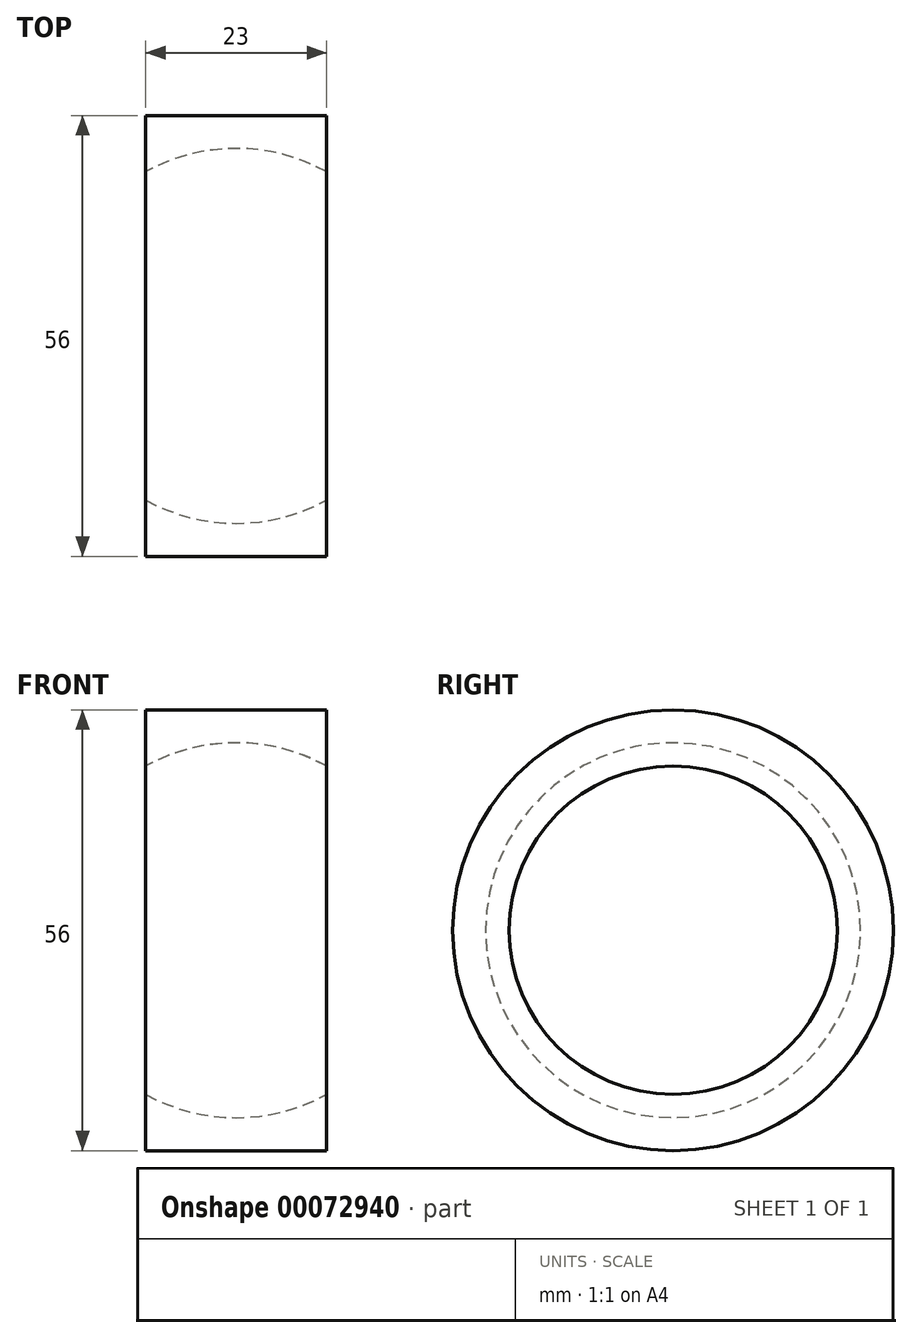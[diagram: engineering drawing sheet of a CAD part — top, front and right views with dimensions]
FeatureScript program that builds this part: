
annotation { "Feature Type Name" : "Feature", "Feature Type Description" : "" }
export const myFeature = defineFeature(function(context is Context, id is Id, definition is map)
    precondition{}
    {
        {
            var Q0;
            Q0=qCreatedBy(makeId("Top.planeOp"),FACE);
            var sketch = newSketch(context, id + "F0", { "sketchPlane" : qUnion([Q0])});
            skArc(sketch, "E0", {"start": v(11.5, 20.85) * mm, "mid": v(0, 23.81) * mm, "end": v(-11.5, 20.85) * mm});
            skLineSegment(sketch, "E1", {"start": v(-11.5, 20.85) * mm, "end": v(-11.5, 28) * mm});
            skLineSegment(sketch, "E2", {"start": v(-11.5, 28) * mm, "end": v(11.5, 28) * mm});
            skLineSegment(sketch, "E3", {"start": v(11.5, 28) * mm, "end": v(11.5, 20.85) * mm});
            skLineSegment(sketch, "E4", {"start": v(-56.58, 0) * mm, "end": v(56, 0) * mm, "construction": true});
            skSolve(sketch);
        }
        {
            var Q0;
            {var subQ1=sQuery(id+"F0.wireOp",EDGE,"E1");Q0=makeQuery(id+"F0.imprint","IMPRINT",FACE,{"disambiguationData":[TD([[makeQuery(id+"F0.imprint","IMPRINT",EDGE,{"derivedFrom":subQ1}),-1.0]])]});}
            var Q1;
            {var subQ0=sQuery(id+"F0.wireOp",EDGE,"7581acdf-5fe9-4c53-8079-498f3a8d60e3");Q1=makeQuery(id+"F0.imprint","IMPRINT",FACE,{"disambiguationData":[TD([[makeQuery(id+"F0.imprint","IMPRINT",EDGE,{"derivedFrom":subQ0}),-1.0]])]});}
            var Q2;
            Q2=sQuery(id+"F0.wireOp",EDGE,"E4");
            revolve(context, id + "F1", {"entities" : qUnion([Q0, Q1]), "axis" : qUnion([Q2]), "revolveType" : RevolveType.FULL});
        }
    });
